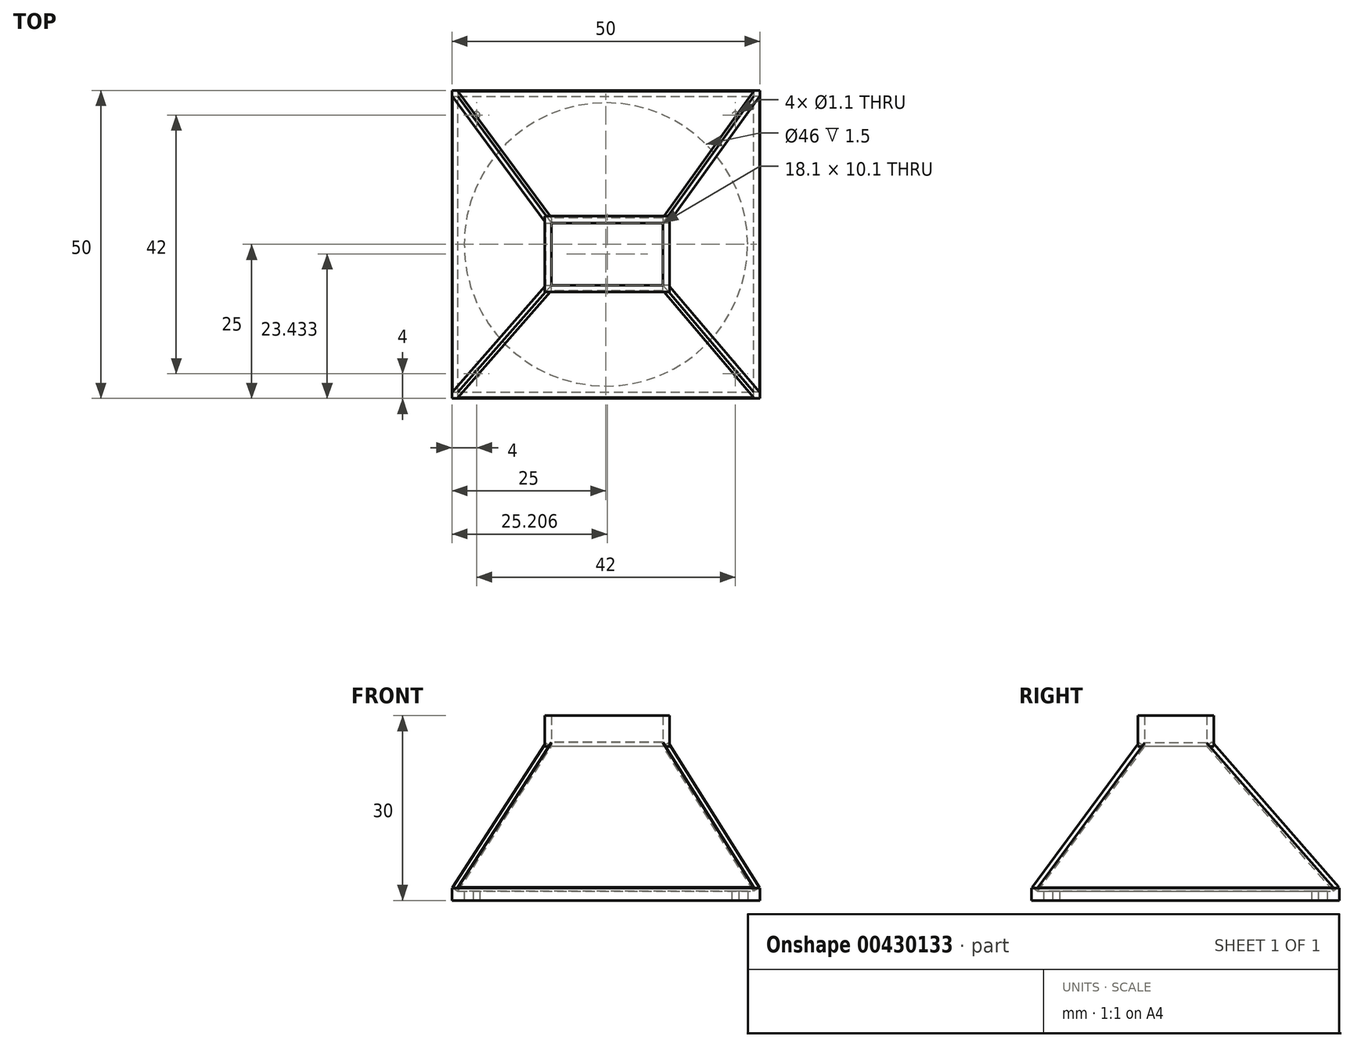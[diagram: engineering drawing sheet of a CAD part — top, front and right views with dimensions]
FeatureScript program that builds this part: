
annotation { "Feature Type Name" : "Feature", "Feature Type Description" : "" }
export const myFeature = defineFeature(function(context is Context, id is Id, definition is map)
    precondition{}
    {
        {
            var Q0;
            Q0=qCreatedBy(makeId("Top.planeOp"),FACE);
            var sketch = newSketch(context, id + "F0", { "sketchPlane" : qUnion([Q0])});
            skPoint(sketch, "E0.middle", {"position": v(0, 0) * mm});
            skLineSegment(sketch, "E1", {"start": v(0, 67.8) * mm, "end": v(0, -53.77) * mm, "construction": true});
            skCircle(sketch, "E2", {"center": v(0, 0) * mm, "radius": 23 * mm});
            skLineSegment(sketch, "E3.bottom", {"start": v(25, 25) * mm, "end": v(-25, 25) * mm});
            skLineSegment(sketch, "E3.top", {"start": v(25, -25) * mm, "end": v(-25, -25) * mm});
            skLineSegment(sketch, "E3.left", {"start": v(25, 25) * mm, "end": v(25, -25) * mm});
            skLineSegment(sketch, "E3.right", {"start": v(-25, 25) * mm, "end": v(-25, -25) * mm});
            skCircle(sketch, "E4", {"center": v(21, 21) * mm, "radius": 0.55 * mm});
            skCircle(sketch, "E5.MirrorC", {"center": v(-21, 21) * mm, "radius": 0.55 * mm});
            skCircle(sketch, "E6.MirrorC", {"center": v(-21, -21) * mm, "radius": 0.55 * mm});
            skCircle(sketch, "E7.MirrorC", {"center": v(21, -21) * mm, "radius": 0.55 * mm});
            skLineSegment(sketch, "E8.0", {"start": v(24, 24) * mm, "end": v(24, -24) * mm});
            skLineSegment(sketch, "E8.1", {"start": v(24, 24) * mm, "end": v(-24, 24) * mm});
            skLineSegment(sketch, "E8.2", {"start": v(-24, 24) * mm, "end": v(-24, -24) * mm});
            skLineSegment(sketch, "E8.3", {"start": v(24, -24) * mm, "end": v(-24, -24) * mm});
            skPoint(sketch, "E0.right.end.orphan", {"position": v(-9.05, -5.05) * mm});
            skPoint(sketch, "E9.orphan", {"position": v(-9.05, 5.05) * mm});
            skPoint(sketch, "E0.left.end.orphan", {"position": v(9.05, -5.05) * mm});
            skPoint(sketch, "E0.left.start.orphan", {"position": v(9.05, 5.05) * mm});
            skSolve(sketch);
        }
        {
            var Q0;
            Q0 = qSketchRegion(id + "F0", true);
            var Q1;
            Q1=makeQuery(id+"F0.imprint","IMPRINT",FACE,{"disambiguationData":[TD([[makeQuery(id+"F0.imprint","IMPRINT",EDGE,{"derivedFrom":sQuery(id+"F0.wireOp",EDGE,"E2")}),-1.0]])]});
            extrude(context, id + "F1", {"entities" : qUnion([Q0, Q1]), "depth" : 1.5 * mm});
        }
        {
            var Q0;
            Q0=qCreatedBy(makeId("Top.planeOp"),FACE);
            cPlane(context, id + "F2", {"entities" : qUnion([Q0]), "cplaneType" : CPlaneType.OFFSET, "offset" : 25 * mm, "width" : 150 * mm, "height" : 150 * mm});
        }
        {
            var Q0;
            Q0=qCreatedBy(id+"F2.planeOp",FACE);
            var sketch = newSketch(context, id + "F3", { "sketchPlane" : qUnion([Q0])});
            skLineSegment(sketch, "E10.bottom", {"start": v(9.26, 3.48) * mm, "end": v(-8.84, 3.48) * mm});
            skLineSegment(sketch, "E10.top", {"start": v(9.26, -6.62) * mm, "end": v(-8.84, -6.62) * mm});
            skLineSegment(sketch, "E10.left", {"start": v(9.26, 3.48) * mm, "end": v(9.26, -6.62) * mm});
            skLineSegment(sketch, "E10.right", {"start": v(-8.84, 3.48) * mm, "end": v(-8.84, -6.62) * mm});
            skPoint(sketch, "E10.middle", {"position": v(0.2, -1.57) * mm});
            skLineSegment(sketch, "E11", {"start": v(0.2, 66.24) * mm, "end": v(0.2, -55.34) * mm, "construction": true});
            skLineSegment(sketch, "E12.0", {"start": v(-9.94, 4.58) * mm, "end": v(-9.94, -7.72) * mm});
            skLineSegment(sketch, "E12.1", {"start": v(10.36, 4.58) * mm, "end": v(-9.94, 4.58) * mm});
            skLineSegment(sketch, "E12.2", {"start": v(10.36, 4.58) * mm, "end": v(10.36, -7.72) * mm});
            skLineSegment(sketch, "E12.3", {"start": v(10.36, -7.72) * mm, "end": v(-9.94, -7.72) * mm});
            skSolve(sketch);
        }
        {
            var Q0;
            Q0=makeQuery(id+"F3.imprint","IMPRINT",FACE,{"disambiguationData":[TD([[makeQuery(id+"F3.imprint","IMPRINT",EDGE,{"derivedFrom":sQuery(id+"F3.wireOp",EDGE,"E10.bottom")}),-1.0]])]});
            extrude(context, id + "F4", {"entities" : qUnion([Q0]), "depth" : 5 * mm});
        }
        {
            var Q0;
            Q0 = qSketchRegion(id + "F0", true);
            extrude(context, id + "F5", {"entities" : qUnion([Q0]), "operationType" : NewBodyOperationType.ADD, "depth" : 2 * mm});
        }
        {
            var Q0;
            Q0=makeQuery(id+"F5.opExtrude","SWEPT_FACE",FACE,{"disambiguationData":[OSD([sQuery(id+"F0.wireOp",EDGE,"E8.0")])]});
            var Q1;
            Q1=makeQuery(id+"F5.boolean.opBoolean","INTERSECT",EDGE,{"derivedFrom":[makeQuery(id+"F1.opExtrude","CAP_FACE",FACE,{"disambiguationData":[OSD([sQuery(id+"F0.wireOp",EDGE,"E2"),sQuery(id+"F0.wireOp",EDGE,"E3.bottom"),sQuery(id+"F0.wireOp",EDGE,"E3.top"),sQuery(id+"F0.wireOp",EDGE,"E3.left"),sQuery(id+"F0.wireOp",EDGE,"E3.right"),sQuery(id+"F0.wireOp",EDGE,"E4"),sQuery(id+"F0.wireOp",EDGE,"E5.MirrorC"),sQuery(id+"F0.wireOp",EDGE,"E6.MirrorC"),sQuery(id+"F0.wireOp",EDGE,"E7.MirrorC")])],"isStart":false}),makeQuery(id+"F5.opExtrude","SWEPT_FACE",FACE,{"disambiguationData":[OSD([sQuery(id+"F0.wireOp",EDGE,"E8.0")])]})]});
            var Q2;
            Q2=sQuery(id+"F3.wireOp",EDGE,"E10.left");
            loft(context, id + "F6", {"bodyType" : ToolBodyType.SURFACE, "sheetProfilesArray" : [{ "sheetProfileEntities" : qUnion([Q0]) }], "wireProfilesArray" : [{ "wireProfileEntities" : qUnion([Q1]) }, { "wireProfileEntities" : qUnion([Q2]) }]});
        }
        {
            var Q0;
            Q0=makeQuery(id+"F6.opLoft","SWEPT_FACE",FACE,{"disambiguationData":[OSD([sQuery(id+"F0.wireOp",EDGE,"E2"),sQuery(id+"F0.wireOp",EDGE,"E3.bottom"),sQuery(id+"F0.wireOp",EDGE,"E3.top"),sQuery(id+"F0.wireOp",EDGE,"E3.left"),sQuery(id+"F0.wireOp",EDGE,"E3.right"),sQuery(id+"F0.wireOp",EDGE,"E4"),sQuery(id+"F0.wireOp",EDGE,"E5.MirrorC"),sQuery(id+"F0.wireOp",EDGE,"E6.MirrorC"),sQuery(id+"F0.wireOp",EDGE,"E7.MirrorC"),sQuery(id+"F0.wireOp",EDGE,"E8.0"),sQuery(id+"F0.wireOp",EDGE,"E8.1"),sQuery(id+"F0.wireOp",EDGE,"E8.3"),sQuery(id+"F3.wireOp",VERTEX,"E10.left.start"),sQuery(id+"F3.wireOp",VERTEX,"E10.left.end"),sQuery(id+"F3.wireOp",EDGE,"E10.left")])]});
            extrude(context, id + "F7", {"entities" : qUnion([Q0]), "oppositeDirection" : true, "depth" : 1.1 * mm});
        }
        {
            var Q0;
            Q0=sQuery(id+"F3.wireOp",EDGE,"E10.bottom");
            var Q1;
            Q1=makeQuery(id+"F5.boolean.opBoolean","INTERSECT",EDGE,{"derivedFrom":[makeQuery(id+"F1.opExtrude","CAP_FACE",FACE,{"disambiguationData":[OSD([sQuery(id+"F0.wireOp",EDGE,"E2"),sQuery(id+"F0.wireOp",EDGE,"E3.bottom"),sQuery(id+"F0.wireOp",EDGE,"E3.top"),sQuery(id+"F0.wireOp",EDGE,"E3.left"),sQuery(id+"F0.wireOp",EDGE,"E3.right"),sQuery(id+"F0.wireOp",EDGE,"E4"),sQuery(id+"F0.wireOp",EDGE,"E5.MirrorC"),sQuery(id+"F0.wireOp",EDGE,"E6.MirrorC"),sQuery(id+"F0.wireOp",EDGE,"E7.MirrorC")])],"isStart":false}),makeQuery(id+"F5.opExtrude","SWEPT_FACE",FACE,{"disambiguationData":[OSD([sQuery(id+"F0.wireOp",EDGE,"E8.1")])]})]});
            loft(context, id + "F8", {"bodyType" : ToolBodyType.SURFACE, "wireProfilesArray" : [{ "wireProfileEntities" : qUnion([Q0]) }, { "wireProfileEntities" : qUnion([Q1]) }]});
        }
        {
            var Q0;
            Q0=makeQuery(id+"F8.opLoft","SWEPT_FACE",FACE,{"disambiguationData":[OSD([sQuery(id+"F0.wireOp",EDGE,"E2"),sQuery(id+"F0.wireOp",EDGE,"E3.bottom"),sQuery(id+"F0.wireOp",EDGE,"E3.top"),sQuery(id+"F0.wireOp",EDGE,"E3.left"),sQuery(id+"F0.wireOp",EDGE,"E3.right"),sQuery(id+"F0.wireOp",EDGE,"E4"),sQuery(id+"F0.wireOp",EDGE,"E5.MirrorC"),sQuery(id+"F0.wireOp",EDGE,"E6.MirrorC"),sQuery(id+"F0.wireOp",EDGE,"E7.MirrorC"),sQuery(id+"F0.wireOp",EDGE,"E8.0"),sQuery(id+"F0.wireOp",EDGE,"E8.1"),sQuery(id+"F0.wireOp",EDGE,"E8.2"),sQuery(id+"F3.wireOp",VERTEX,"E10.bottom.start"),sQuery(id+"F3.wireOp",VERTEX,"E10.bottom.end"),sQuery(id+"F3.wireOp",EDGE,"E10.bottom")])]});
            extrude(context, id + "F9", {"entities" : qUnion([Q0]), "oppositeDirection" : true, "depth" : 1.1 * mm});
        }
        {
            var Q0;
            Q0=makeQuery(id+"F5.boolean.opBoolean","INTERSECT",EDGE,{"derivedFrom":[makeQuery(id+"F1.opExtrude","CAP_FACE",FACE,{"disambiguationData":[OSD([sQuery(id+"F0.wireOp",EDGE,"E2"),sQuery(id+"F0.wireOp",EDGE,"E3.bottom"),sQuery(id+"F0.wireOp",EDGE,"E3.top"),sQuery(id+"F0.wireOp",EDGE,"E3.left"),sQuery(id+"F0.wireOp",EDGE,"E3.right"),sQuery(id+"F0.wireOp",EDGE,"E4"),sQuery(id+"F0.wireOp",EDGE,"E5.MirrorC"),sQuery(id+"F0.wireOp",EDGE,"E6.MirrorC"),sQuery(id+"F0.wireOp",EDGE,"E7.MirrorC")])],"isStart":false}),makeQuery(id+"F5.opExtrude","SWEPT_FACE",FACE,{"disambiguationData":[OSD([sQuery(id+"F0.wireOp",EDGE,"E8.2")])]})]});
            var Q1;
            Q1=sQuery(id+"F3.wireOp",EDGE,"E10.right");
            loft(context, id + "F10", {"bodyType" : ToolBodyType.SURFACE, "wireProfilesArray" : [{ "wireProfileEntities" : qUnion([Q0]) }, { "wireProfileEntities" : qUnion([Q1]) }]});
        }
        {
            var Q0;
            Q0=makeQuery(id+"F10.opLoft","SWEPT_FACE",FACE,{"disambiguationData":[OSD([sQuery(id+"F0.wireOp",VERTEX,"E3.right.start"),sQuery(id+"F0.wireOp",VERTEX,"E3.right.end"),sQuery(id+"F0.wireOp",EDGE,"E3.right"),sQuery(id+"F3.wireOp",VERTEX,"E10.right.start"),sQuery(id+"F3.wireOp",VERTEX,"E10.right.end"),sQuery(id+"F3.wireOp",EDGE,"E10.right")])]});
            extrude(context, id + "F11", {"entities" : qUnion([Q0]), "depth" : 1.1 * mm});
        }
        {
            var Q0;
            Q0=makeQuery(id+"F5.boolean.opBoolean","INTERSECT",EDGE,{"derivedFrom":[makeQuery(id+"F1.opExtrude","CAP_FACE",FACE,{"disambiguationData":[OSD([sQuery(id+"F0.wireOp",EDGE,"E2"),sQuery(id+"F0.wireOp",EDGE,"E3.bottom"),sQuery(id+"F0.wireOp",EDGE,"E3.top"),sQuery(id+"F0.wireOp",EDGE,"E3.left"),sQuery(id+"F0.wireOp",EDGE,"E3.right"),sQuery(id+"F0.wireOp",EDGE,"E4"),sQuery(id+"F0.wireOp",EDGE,"E5.MirrorC"),sQuery(id+"F0.wireOp",EDGE,"E6.MirrorC"),sQuery(id+"F0.wireOp",EDGE,"E7.MirrorC")])],"isStart":false}),makeQuery(id+"F5.opExtrude","SWEPT_FACE",FACE,{"disambiguationData":[OSD([sQuery(id+"F0.wireOp",EDGE,"E8.3")])]})]});
            var Q1;
            Q1=sQuery(id+"F3.wireOp",EDGE,"E10.top");
            loft(context, id + "F12", {"bodyType" : ToolBodyType.SURFACE, "wireProfilesArray" : [{ "wireProfileEntities" : qUnion([Q0]) }, { "wireProfileEntities" : qUnion([Q1]) }]});
        }
        {
            var Q0;
            Q0=makeQuery(id+"F12.opLoft","SWEPT_FACE",FACE,{"disambiguationData":[OSD([sQuery(id+"F0.wireOp",EDGE,"E2"),sQuery(id+"F0.wireOp",EDGE,"E3.bottom"),sQuery(id+"F0.wireOp",EDGE,"E3.top"),sQuery(id+"F0.wireOp",EDGE,"E3.left"),sQuery(id+"F0.wireOp",EDGE,"E3.right"),sQuery(id+"F0.wireOp",EDGE,"E4"),sQuery(id+"F0.wireOp",EDGE,"E5.MirrorC"),sQuery(id+"F0.wireOp",EDGE,"E6.MirrorC"),sQuery(id+"F0.wireOp",EDGE,"E7.MirrorC"),sQuery(id+"F0.wireOp",EDGE,"E8.0"),sQuery(id+"F0.wireOp",EDGE,"E8.2"),sQuery(id+"F0.wireOp",EDGE,"E8.3"),sQuery(id+"F3.wireOp",VERTEX,"E10.top.start"),sQuery(id+"F3.wireOp",VERTEX,"E10.top.end"),sQuery(id+"F3.wireOp",EDGE,"E10.top")])]});
            extrude(context, id + "F13", {"entities" : qUnion([Q0]), "oppositeDirection" : true, "depth" : 1.1 * mm});
        }
    });
